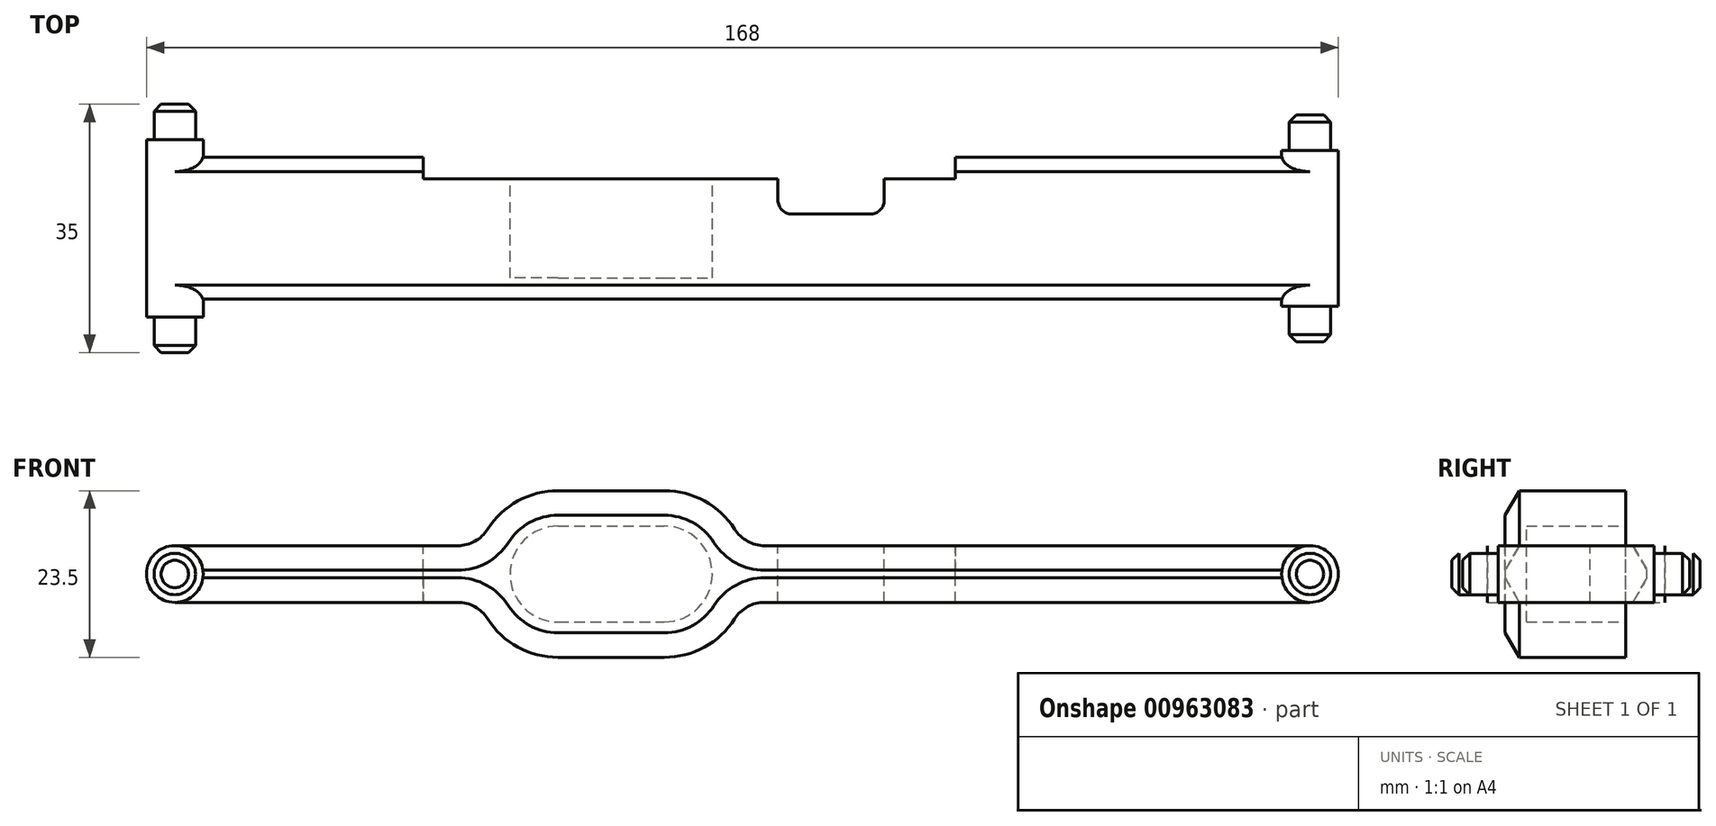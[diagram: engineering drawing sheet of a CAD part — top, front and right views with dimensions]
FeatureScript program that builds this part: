
annotation { "Feature Type Name" : "Feature", "Feature Type Description" : "" }
export const myFeature = defineFeature(function(context is Context, id is Id, definition is map)
    precondition{}
    {
        {
            var Q0;
            Q0=qCreatedBy(makeId("Front.planeOp"),FACE);
            var sketch = newSketch(context, id + "F0", { "sketchPlane" : qUnion([Q0])});
            skCircle(sketch, "E0", {"center": v(0, 0) * mm, "radius": 2.93 * mm});
            skSolve(sketch);
        }
        {
            var Q0;
            Q0 = qSketchRegion(id + "F0", true);
            extrude(context, id + "F1", {"entities" : qUnion([Q0]), "depth" : 32 * mm, "offsetDistance" : 25 * mm, "symmetric" : true});
        }
        {
            var Q0;
            Q0=qCreatedBy(makeId("Front.planeOp"),FACE);
            var sketch = newSketch(context, id + "F2", { "sketchPlane" : qUnion([Q0])});
            skCircle(sketch, "E1", {"center": v(-160, 0) * mm, "radius": 2.93 * mm});
            skSolve(sketch);
        }
        {
            var Q0;
            Q0 = qSketchRegion(id + "F2", true);
            extrude(context, id + "F3", {"entities" : qUnion([Q0]), "depth" : 35 * mm, "offsetDistance" : 25 * mm, "symmetric" : true});
        }
        {
            var Q0;
            Q0=qCreatedBy(makeId("Front.planeOp"),FACE);
            var sketch = newSketch(context, id + "F4", { "sketchPlane" : qUnion([Q0])});
            skCircle(sketch, "E2", {"center": v(0, 0) * mm, "radius": 4 * mm});
            skSolve(sketch);
        }
        {
            var Q0;
            Q0 = qSketchRegion(id + "F4", true);
            extrude(context, id + "F5", {"entities" : qUnion([Q0]), "operationType" : NewBodyOperationType.ADD, "depth" : 22 * mm, "offsetDistance" : 25 * mm, "symmetric" : true});
        }
        {
            var Q0;
            Q0=qCreatedBy(makeId("Front.planeOp"),FACE);
            var sketch = newSketch(context, id + "F6", { "sketchPlane" : qUnion([Q0])});
            skCircle(sketch, "E3", {"center": v(-160, 0) * mm, "radius": 4 * mm});
            skSolve(sketch);
        }
        {
            var Q0;
            Q0 = qSketchRegion(id + "F6", true);
            extrude(context, id + "F7", {"entities" : qUnion([Q0]), "operationType" : NewBodyOperationType.ADD, "depth" : 25 * mm, "offsetDistance" : 25 * mm, "symmetric" : true});
        }
        {
            var Q0;
            Q0=qCreatedBy(makeId("Front.planeOp"),FACE);
            var sketch = newSketch(context, id + "F8", { "sketchPlane" : qUnion([Q0])});
            skLineSegment(sketch, "E4.bottom", {"start": v(-160, 4) * mm, "end": v(0, 4) * mm});
            skLineSegment(sketch, "E4.top", {"start": v(-160, -4) * mm, "end": v(0, -4) * mm});
            skLineSegment(sketch, "E4.left", {"start": v(-160, 4) * mm, "end": v(-160, -4) * mm});
            skLineSegment(sketch, "E4.right", {"start": v(0, 4) * mm, "end": v(0, -4) * mm});
            skSolve(sketch);
        }
        {
            var Q0;
            Q0 = qSketchRegion(id + "F8", true);
            extrude(context, id + "F9", {"entities" : qUnion([Q0]), "operationType" : NewBodyOperationType.ADD, "depth" : 20 * mm, "offsetDistance" : 25 * mm, "symmetric" : true});
        }
        {
            var Q0;
            Q0=qCreatedBy(makeId("Front.planeOp"),FACE);
            var sketch = newSketch(context, id + "F10", { "sketchPlane" : qUnion([Q0])});
            skArc(sketch, "E5", {"start": v(-106, 6.75) * mm, "mid": v(-112.75, 0) * mm, "end": v(-106, -6.75) * mm});
            skArc(sketch, "E6", {"start": v(-91, -6.75) * mm, "mid": v(-84.25, 0) * mm, "end": v(-91, 6.75) * mm});
            skLineSegment(sketch, "E7", {"start": v(-106, 6.75) * mm, "end": v(-91, 6.75) * mm});
            skLineSegment(sketch, "E8", {"start": v(-106, -6.75) * mm, "end": v(-91, -6.75) * mm});
            skLineSegment(sketch, "E9.0", {"start": v(-106, 11.75) * mm, "end": v(-91, 11.75) * mm});
            skArc(sketch, "E9.1", {"start": v(-106, 11.75) * mm, "mid": v(-117.75, 0) * mm, "end": v(-106, -11.75) * mm});
            skLineSegment(sketch, "E9.2", {"start": v(-106, -11.75) * mm, "end": v(-91, -11.75) * mm});
            skArc(sketch, "E9.3", {"start": v(-91, -11.75) * mm, "mid": v(-79.25, 0) * mm, "end": v(-91, 11.75) * mm});
            skSolve(sketch);
        }
        {
            var Q0;
            Q0 = qSketchRegion(id + "F10", true);
            var Q1;
            Q1=makeQuery(id+"F9.opExtrude","CAP_FACE",FACE,{"disambiguationData":[OSD([sQuery(id+"F8.wireOp",EDGE,"E4.bottom"),sQuery(id+"F8.wireOp",EDGE,"E4.top"),sQuery(id+"F8.wireOp",EDGE,"E4.left"),sQuery(id+"F8.wireOp",EDGE,"E4.right")])],"isStart":false});
            var Q2;
            Q2=makeQuery(id+"F9.opExtrude","CAP_FACE",FACE,{"disambiguationData":[OSD([sQuery(id+"F8.wireOp",EDGE,"E4.bottom"),sQuery(id+"F8.wireOp",EDGE,"E4.top"),sQuery(id+"F8.wireOp",EDGE,"E4.left"),sQuery(id+"F8.wireOp",EDGE,"E4.right")])],"isStart":true});
            extrude(context, id + "F11", {"entities" : qUnion([Q0]), "operationType" : NewBodyOperationType.ADD, "endBound" : BoundingType.UP_TO_SURFACE, "depth" : 25 * mm, "endBoundEntityFace" : qUnion([Q1]), "offsetDistance" : 25 * mm, "hasSecondDirection" : true, "secondDirectionBound" : BoundingType.UP_TO_SURFACE, "secondDirectionOppositeDirection" : true, "secondDirectionDepth" : 25 * mm, "secondDirectionBoundEntityFace" : qUnion([Q2])});
        }
        {
            var Q0;
            Q0=qCreatedBy(makeId("Front.planeOp"),FACE);
            var sketch = newSketch(context, id + "F12", { "sketchPlane" : qUnion([Q0])});
            skArc(sketch, "E10.0", {"start": v(-106, 6.75) * mm, "mid": v(-112.75, 0) * mm, "end": v(-106, -6.75) * mm});
            skLineSegment(sketch, "E10.1", {"start": v(-106, 6.75) * mm, "end": v(-91, 6.75) * mm});
            skArc(sketch, "E10.2", {"start": v(-91, -6.75) * mm, "mid": v(-84.25, 0) * mm, "end": v(-91, 6.75) * mm});
            skLineSegment(sketch, "E10.3", {"start": v(-106, -6.75) * mm, "end": v(-91, -6.75) * mm});
            skSolve(sketch);
        }
        {
            var Q0;
            Q0 = qSketchRegion(id + "F12", true);
            extrude(context, id + "F13", {"entities" : qUnion([Q0]), "operationType" : NewBodyOperationType.REMOVE, "endBound" : BoundingType.THROUGH_ALL, "oppositeDirection" : true, "depth" : 25 * mm, "offsetDistance" : 25 * mm, "hasSecondDirection" : true, "secondDirectionBound" : BoundingType.THROUGH_ALL, "secondDirectionOppositeDirection" : false, "secondDirectionDepth" : 25 * mm});
        }
        {
            var Q0;
            Q0=makeQuery(id+"F11.boolean.opBoolean","MERGE",FACE,{"derivedFrom":[makeQuery(id+"F9.opExtrude","CAP_FACE",FACE,{"disambiguationData":[OSD([sQuery(id+"F8.wireOp",EDGE,"E4.bottom"),sQuery(id+"F8.wireOp",EDGE,"E4.top"),sQuery(id+"F8.wireOp",EDGE,"E4.left"),sQuery(id+"F8.wireOp",EDGE,"E4.right")])],"isStart":false}),makeQuery(id+"F11.opExtrude","CAP_FACE",FACE,{"disambiguationData":[OSD([sQuery(id+"F10.wireOp",EDGE,"E5"),sQuery(id+"F10.wireOp",EDGE,"E6"),sQuery(id+"F10.wireOp",EDGE,"E7"),sQuery(id+"F10.wireOp",EDGE,"E8"),sQuery(id+"F10.wireOp",EDGE,"E9.0"),sQuery(id+"F10.wireOp",EDGE,"E9.1"),sQuery(id+"F10.wireOp",EDGE,"E9.2"),sQuery(id+"F10.wireOp",EDGE,"E9.3")])],"isStart":false})]});
            var sketch = newSketch(context, id + "F14", { "sketchPlane" : qUnion([Q0])});
            skArc(sketch, "E11.0", {"start": v(-106, 6.75) * mm, "mid": v(-112.75, 0) * mm, "end": v(-106, -6.75) * mm});
            skLineSegment(sketch, "E11.1", {"start": v(-106, 6.75) * mm, "end": v(-91, 6.75) * mm});
            skArc(sketch, "E11.2", {"start": v(-91, -6.75) * mm, "mid": v(-84.25, 0) * mm, "end": v(-91, 6.75) * mm});
            skLineSegment(sketch, "E11.3", {"start": v(-106, -6.75) * mm, "end": v(-91, -6.75) * mm});
            skSolve(sketch);
        }
        {
            var Q0;
            Q0 = qSketchRegion(id + "F14", true);
            extrude(context, id + "F15", {"entities" : qUnion([Q0]), "operationType" : NewBodyOperationType.ADD, "oppositeDirection" : true, "depth" : 3 * mm, "offsetDistance" : 25 * mm});
        }
        {
            var Q0;
            Q0=qCreatedBy(makeId("Top.planeOp"),FACE);
            var sketch = newSketch(context, id + "F16", { "sketchPlane" : qUnion([Q0])});
            skLineSegment(sketch, "E12.bottom", {"start": v(-125, 10) * mm, "end": v(-50, 10) * mm});
            skLineSegment(sketch, "E12.top", {"start": v(-125, 7) * mm, "end": v(-50, 7) * mm});
            skLineSegment(sketch, "E12.left", {"start": v(-125, 10) * mm, "end": v(-125, 7) * mm});
            skLineSegment(sketch, "E12.right", {"start": v(-50, 10) * mm, "end": v(-50, 7) * mm});
            skSolve(sketch);
        }
        {
            var Q0;
            Q0 = qSketchRegion(id + "F16", true);
            extrude(context, id + "F17", {"entities" : qUnion([Q0]), "operationType" : NewBodyOperationType.REMOVE, "endBound" : BoundingType.UP_TO_NEXT, "oppositeDirection" : true, "depth" : 25 * mm, "offsetDistance" : 25 * mm, "hasSecondDirection" : true, "secondDirectionBound" : BoundingType.UP_TO_NEXT, "secondDirectionOppositeDirection" : false, "secondDirectionDepth" : 25 * mm});
        }
        {
            var Q0;
            Q0=makeQuery(id+"F11.boolean.opBoolean","INTERSECT",EDGE,{"derivedFrom":[makeQuery(id+"F9.opExtrude","SWEPT_FACE",FACE,{"disambiguationData":[OSD([sQuery(id+"F8.wireOp",EDGE,"E4.bottom")])]}),makeQuery(id+"F11.opExtrude","SWEPT_FACE",FACE,{"disambiguationData":[OSD([sQuery(id+"F10.wireOp",EDGE,"E9.1")])]})]});
            var Q1;
            Q1=makeQuery(id+"F11.boolean.opBoolean","INTERSECT",EDGE,{"derivedFrom":[makeQuery(id+"F9.opExtrude","SWEPT_FACE",FACE,{"disambiguationData":[OSD([sQuery(id+"F8.wireOp",EDGE,"E4.top")])]}),makeQuery(id+"F11.opExtrude","SWEPT_FACE",FACE,{"disambiguationData":[OSD([sQuery(id+"F10.wireOp",EDGE,"E9.1")])]})]});
            var Q2;
            Q2=makeQuery(id+"F11.boolean.opBoolean","INTERSECT",EDGE,{"derivedFrom":[makeQuery(id+"F9.opExtrude","SWEPT_FACE",FACE,{"disambiguationData":[OSD([sQuery(id+"F8.wireOp",EDGE,"E4.top")])]}),makeQuery(id+"F11.opExtrude","SWEPT_FACE",FACE,{"disambiguationData":[OSD([sQuery(id+"F10.wireOp",EDGE,"E9.3")])]})]});
            var Q3;
            Q3=makeQuery(id+"F11.boolean.opBoolean","INTERSECT",EDGE,{"derivedFrom":[makeQuery(id+"F9.opExtrude","SWEPT_FACE",FACE,{"disambiguationData":[OSD([sQuery(id+"F8.wireOp",EDGE,"E4.bottom")])]}),makeQuery(id+"F11.opExtrude","SWEPT_FACE",FACE,{"disambiguationData":[OSD([sQuery(id+"F10.wireOp",EDGE,"E9.3")])]})]});
            fillet(context, id + "F18", {"entities" : qUnion([Q0, Q1, Q2, Q3]), "tangentPropagation" : true, "radius" : 5 * mm, "defaultsChanged" : false, "vertexSettings" : [], "allowEdgeOverflow" : false});
        }
        {
            var Q0;
            {var subQ1=sQuery(id+"F8.wireOp",EDGE,"E4.top");Q0=makeQuery(id+"F11.boolean.opBoolean","SPLIT",EDGE,{"disambiguationData":[TD([makeQuery(id+"F5.opExtrude","SWEPT_FACE",FACE,{"disambiguationData":[OSD([sQuery(id+"F4.wireOp",EDGE,"E2")])]})])],"derivedFrom":makeQuery(id+"F9.opExtrude","CAP_EDGE",EDGE,{"disambiguationData":[OSD([subQ1])],"isStart":true})});}
            var Q1;
            {var subQ1=sQuery(id+"F8.wireOp",EDGE,"E4.top");Q1=makeQuery(id+"F11.boolean.opBoolean","SPLIT",EDGE,{"disambiguationData":[TD([makeQuery(id+"F7.opExtrude","SWEPT_FACE",FACE,{"disambiguationData":[OSD([sQuery(id+"F6.wireOp",EDGE,"E3")])]})])],"derivedFrom":makeQuery(id+"F9.opExtrude","CAP_EDGE",EDGE,{"disambiguationData":[OSD([subQ1])],"isStart":true})});}
            var Q2;
            {var subQ0=sQuery(id+"F8.wireOp",EDGE,"E4.bottom");Q2=makeQuery(id+"F11.boolean.opBoolean","SPLIT",EDGE,{"disambiguationData":[TD([makeQuery(id+"F7.opExtrude","SWEPT_FACE",FACE,{"disambiguationData":[OSD([sQuery(id+"F6.wireOp",EDGE,"E3")])]})])],"derivedFrom":makeQuery(id+"F9.opExtrude","CAP_EDGE",EDGE,{"disambiguationData":[OSD([subQ0])],"isStart":false})});}
            var Q3;
            {var subQ0=sQuery(id+"F8.wireOp",EDGE,"E4.bottom");Q3=makeQuery(id+"F11.boolean.opBoolean","SPLIT",EDGE,{"disambiguationData":[TD([makeQuery(id+"F5.opExtrude","SWEPT_FACE",FACE,{"disambiguationData":[OSD([sQuery(id+"F4.wireOp",EDGE,"E2")])]})])],"derivedFrom":makeQuery(id+"F9.opExtrude","CAP_EDGE",EDGE,{"disambiguationData":[OSD([subQ0])],"isStart":true})});}
            chamfer(context, id + "F19", {"entities" : qUnion([Q0, Q1, Q2, Q3]), "chamferType" : ChamferType.OFFSET_ANGLE, "width" : 2 * mm, "oppositeDirection" : false, "angle" : 60 * degree, "tangentPropagation" : true});
        }
        {
            var Q0;
            {var subQ0=sQuery(id+"F8.wireOp",EDGE,"E4.top");Q0=makeQuery(id+"F11.boolean.opBoolean","SPLIT",EDGE,{"disambiguationData":[TD([makeQuery(id+"F7.opExtrude","SWEPT_FACE",FACE,{"disambiguationData":[OSD([sQuery(id+"F6.wireOp",EDGE,"E3")])]})])],"derivedFrom":makeQuery(id+"F9.opExtrude","CAP_EDGE",EDGE,{"disambiguationData":[OSD([subQ0])],"isStart":false})});}
            var Q1;
            {var subQ1=sQuery(id+"F8.wireOp",EDGE,"E4.bottom");Q1=makeQuery(id+"F11.boolean.opBoolean","SPLIT",EDGE,{"disambiguationData":[TD([makeQuery(id+"F7.opExtrude","SWEPT_FACE",FACE,{"disambiguationData":[OSD([sQuery(id+"F6.wireOp",EDGE,"E3")])]})])],"derivedFrom":makeQuery(id+"F9.opExtrude","CAP_EDGE",EDGE,{"disambiguationData":[OSD([subQ1])],"isStart":true})});}
            chamfer(context, id + "F20", {"entities" : qUnion([Q0, Q1]), "chamferType" : ChamferType.OFFSET_ANGLE, "width" : 2 * mm, "oppositeDirection" : true, "angle" : 60 * degree, "tangentPropagation" : true});
        }
        {
            var Q0;
            Q0=qCreatedBy(makeId("Top.planeOp"),FACE);
            var sketch = newSketch(context, id + "F21", { "sketchPlane" : qUnion([Q0])});
            skLineSegment(sketch, "E13.bottom", {"start": v(-75, 7) * mm, "end": v(-60, 7) * mm});
            skLineSegment(sketch, "E13.top", {"start": v(-73, 2) * mm, "end": v(-62, 2) * mm});
            skLineSegment(sketch, "E13.left", {"start": v(-75, 7) * mm, "end": v(-75, 4) * mm});
            skLineSegment(sketch, "E13.right", {"start": v(-60, 7) * mm, "end": v(-60, 4) * mm});
            skPoint(sketch, "E14.visualSharp", {"position": v(-75, 2) * mm});
            skArc(sketch, "E14.filletArc", {"start": v(-75, 4) * mm, "mid": v(-74.41, 2.59) * mm, "end": v(-73, 2) * mm});
            skPoint(sketch, "E15.visualSharp", {"position": v(-60, 2) * mm});
            skArc(sketch, "E15.filletArc", {"start": v(-62, 2) * mm, "mid": v(-60.59, 2.59) * mm, "end": v(-60, 4) * mm});
            skSolve(sketch);
        }
        {
            var Q0;
            Q0 = qSketchRegion(id + "F21", true);
            extrude(context, id + "F22", {"entities" : qUnion([Q0]), "operationType" : NewBodyOperationType.REMOVE, "oppositeDirection" : true, "depth" : 25 * mm, "offsetDistance" : 25 * mm, "symmetric" : true});
        }
        {
            var Q0;
            Q0=makeQuery(id+"F3.opExtrude","CAP_EDGE",EDGE,{"disambiguationData":[OSD([sQuery(id+"F2.wireOp",EDGE,"E1")])],"isStart":true});
            var Q1;
            Q1=makeQuery(id+"F3.opExtrude","CAP_EDGE",EDGE,{"disambiguationData":[OSD([sQuery(id+"F2.wireOp",EDGE,"E1")])],"isStart":false});
            var Q2;
            Q2=makeQuery(id+"F1.opExtrude","CAP_EDGE",EDGE,{"disambiguationData":[OSD([sQuery(id+"F0.wireOp",EDGE,"E0")])],"isStart":true});
            var Q3;
            Q3=makeQuery(id+"F1.opExtrude","CAP_EDGE",EDGE,{"disambiguationData":[OSD([sQuery(id+"F0.wireOp",EDGE,"E0")])],"isStart":false});
            chamfer(context, id + "F23", {"entities" : qUnion([Q0, Q1, Q2, Q3]), "width" : 1 * mm, "tangentPropagation" : true});
        }
    });
